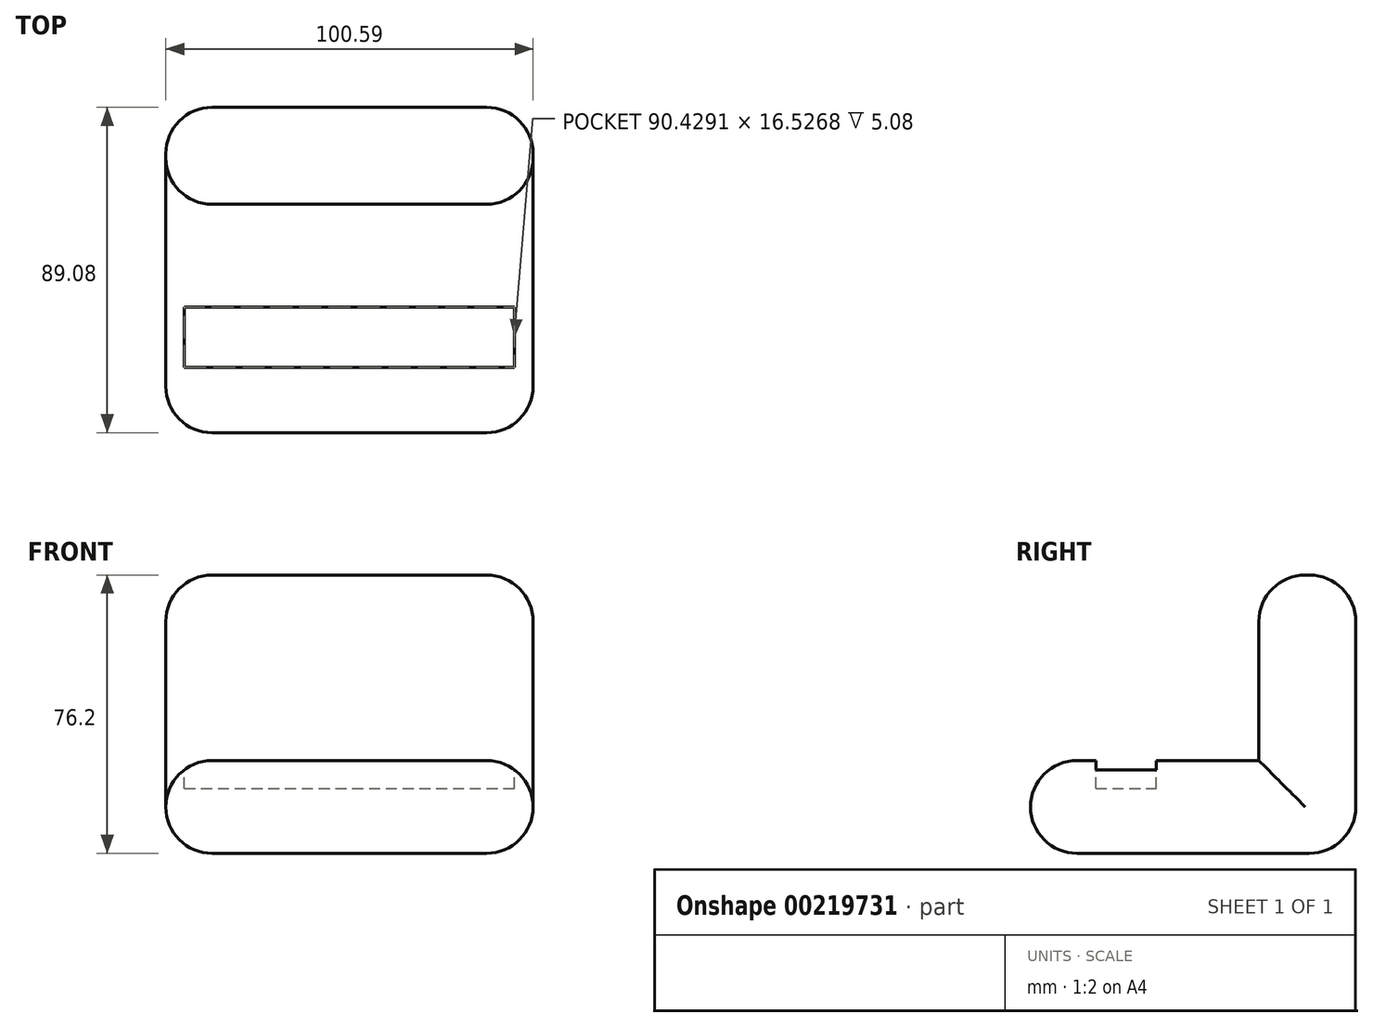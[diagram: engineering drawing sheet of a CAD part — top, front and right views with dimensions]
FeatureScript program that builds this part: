
annotation { "Feature Type Name" : "Feature", "Feature Type Description" : "" }
export const myFeature = defineFeature(function(context is Context, id is Id, definition is map)
    precondition{}
    {
        {
            var Q0;
            Q0=qCreatedBy(makeId("Top.planeOp"),FACE);
            var sketch = newSketch(context, id + "F0", { "sketchPlane" : qUnion([Q0])});
            skLineSegment(sketch, "E0.bottom", {"start": v(-49.16, -34.38) * mm, "end": v(51.43, -34.38) * mm});
            skLineSegment(sketch, "E0.top", {"start": v(-49.16, 54.7) * mm, "end": v(51.43, 54.7) * mm});
            skLineSegment(sketch, "E0.left", {"start": v(-49.16, -34.38) * mm, "end": v(-49.16, 54.7) * mm});
            skLineSegment(sketch, "E0.right", {"start": v(51.43, -34.38) * mm, "end": v(51.43, 54.7) * mm});
            skSolve(sketch);
        }
        {
            var Q0;
            Q0=makeQuery(id+"F0.imprint","IMPRINT",FACE,{"disambiguationData":[TD([[makeQuery(id+"F0.imprint","IMPRINT",EDGE,{"derivedFrom":sQuery(id+"F0.wireOp",EDGE,"E0.bottom")}),1.0]])]});
            extrude(context, id + "F1", {"entities" : qUnion([Q0]), "depth" : 25.4 * mm});
        }
        {
            var Q0;
            Q0=makeQuery(id+"F1.opExtrude","CAP_FACE",FACE,{"disambiguationData":[OSD([sQuery(id+"F0.wireOp",EDGE,"E0.bottom"),sQuery(id+"F0.wireOp",EDGE,"E0.top"),sQuery(id+"F0.wireOp",EDGE,"E0.left"),sQuery(id+"F0.wireOp",EDGE,"E0.right")])],"isStart":false});
            var sketch = newSketch(context, id + "F2", { "sketchPlane" : qUnion([Q0])});
            skLineSegment(sketch, "E1.bottom", {"start": v(-49.16, 28.15) * mm, "end": v(51.43, 28.15) * mm});
            skLineSegment(sketch, "E1.top", {"start": v(-49.16, 54.7) * mm, "end": v(51.43, 54.7) * mm});
            skLineSegment(sketch, "E1.left", {"start": v(-49.16, 28.15) * mm, "end": v(-49.16, 54.7) * mm});
            skLineSegment(sketch, "E1.right", {"start": v(51.43, 28.15) * mm, "end": v(51.43, 54.7) * mm});
            skSolve(sketch);
        }
        {
            var Q0;
            Q0=makeQuery(id+"F2.imprint","IMPRINT",FACE,{"disambiguationData":[TD([[makeQuery(id+"F2.imprint","IMPRINT",EDGE,{"derivedFrom":sQuery(id+"F2.wireOp",EDGE,"E1.bottom")}),1.0]])]});
            extrude(context, id + "F3", {"entities" : qUnion([Q0]), "operationType" : NewBodyOperationType.ADD, "depth" : 50.8 * mm});
        }
        {
            var Q0;
            Q0=makeQuery(id+"F1.opExtrude","CAP_FACE",FACE,{"disambiguationData":[OSD([sQuery(id+"F0.wireOp",EDGE,"E0.bottom"),sQuery(id+"F0.wireOp",EDGE,"E0.top"),sQuery(id+"F0.wireOp",EDGE,"E0.left"),sQuery(id+"F0.wireOp",EDGE,"E0.right")])],"isStart":false});
            var sketch = newSketch(context, id + "F4", { "sketchPlane" : qUnion([Q0])});
            skLineSegment(sketch, "E2.bottom", {"start": v(-44.08, -16.53) * mm, "end": v(46.35, -16.53) * mm});
            skLineSegment(sketch, "E2.top", {"start": v(-44.08, 0) * mm, "end": v(46.35, 0) * mm});
            skLineSegment(sketch, "E2.left", {"start": v(-44.08, -16.53) * mm, "end": v(-44.08, 0) * mm});
            skLineSegment(sketch, "E2.right", {"start": v(46.35, -16.53) * mm, "end": v(46.35, 0) * mm});
            skSolve(sketch);
        }
        {
            var Q0;
            Q0=makeQuery(id+"F4.imprint","IMPRINT",FACE,{"disambiguationData":[TD([[makeQuery(id+"F4.imprint","IMPRINT",EDGE,{"derivedFrom":sQuery(id+"F4.wireOp",EDGE,"E2.bottom")}),1.0]])]});
            extrude(context, id + "F5", {"entities" : qUnion([Q0]), "operationType" : NewBodyOperationType.REMOVE, "oppositeDirection" : true, "depth" : 7.62 * mm});
        }
        {
            var Q0;
            Q0=makeQuery(id+"F1.opExtrude","CAP_EDGE",EDGE,{"disambiguationData":[OSD([sQuery(id+"F0.wireOp",EDGE,"E0.bottom")])],"isStart":false});
            var Q1;
            Q1=makeQuery(id+"F1.opExtrude","SWEPT_EDGE",EDGE,{"disambiguationData":[OSD([sQuery(id+"F0.wireOp",EDGE,"E0.bottom"),sQuery(id+"F0.wireOp",EDGE,"E0.right")])]});
            var Q2;
            Q2=makeQuery(id+"F1.opExtrude","CAP_EDGE",EDGE,{"disambiguationData":[OSD([sQuery(id+"F0.wireOp",EDGE,"E0.bottom")])],"isStart":true});
            var Q3;
            Q3=makeQuery(id+"F1.opExtrude","SWEPT_EDGE",EDGE,{"disambiguationData":[OSD([sQuery(id+"F0.wireOp",EDGE,"E0.bottom"),sQuery(id+"F0.wireOp",EDGE,"E0.left")])]});
            var Q4;
            Q4=makeQuery(id+"F1.opExtrude","CAP_EDGE",EDGE,{"disambiguationData":[OSD([sQuery(id+"F0.wireOp",EDGE,"E0.left")])],"isStart":false});
            var Q5;
            Q5=makeQuery(id+"F3.opExtrude","CAP_EDGE",EDGE,{"disambiguationData":[OSD([sQuery(id+"F2.wireOp",EDGE,"E1.bottom")])],"isStart":false});
            var Q6;
            Q6=makeQuery(id+"F3.opExtrude","SWEPT_EDGE",EDGE,{"disambiguationData":[OSD([sQuery(id+"F0.wireOp",EDGE,"E0.left"),sQuery(id+"F2.wireOp",EDGE,"E1.bottom"),sQuery(id+"F2.wireOp",EDGE,"E1.left")])]});
            var Q7;
            Q7=makeQuery(id+"F3.opExtrude","CAP_EDGE",EDGE,{"disambiguationData":[OSD([sQuery(id+"F2.wireOp",EDGE,"E1.bottom")])],"isStart":true});
            var Q8;
            Q8=makeQuery(id+"F3.opExtrude","SWEPT_EDGE",EDGE,{"disambiguationData":[OSD([sQuery(id+"F0.wireOp",EDGE,"E0.right"),sQuery(id+"F2.wireOp",EDGE,"E1.bottom"),sQuery(id+"F2.wireOp",EDGE,"E1.right")])]});
            var Q9;
            Q9=makeQuery(id+"F1.opExtrude","CAP_EDGE",EDGE,{"disambiguationData":[OSD([sQuery(id+"F0.wireOp",EDGE,"E0.right")])],"isStart":true});
            var Q10;
            Q10=makeQuery(id+"F1.opExtrude","CAP_EDGE",EDGE,{"disambiguationData":[OSD([sQuery(id+"F0.wireOp",EDGE,"E0.right")])],"isStart":false});
            var Q11;
            Q11=makeQuery(id+"F3.boolean.opBoolean","MERGE",EDGE,{"derivedFrom":[makeQuery(id+"F1.opExtrude","SWEPT_EDGE",EDGE,{"disambiguationData":[OSD([sQuery(id+"F0.wireOp",EDGE,"E0.top"),sQuery(id+"F0.wireOp",EDGE,"E0.right")])]}),makeQuery(id+"F3.opExtrude","SWEPT_EDGE",EDGE,{"disambiguationData":[OSD([sQuery(id+"F2.wireOp",EDGE,"E1.top"),sQuery(id+"F2.wireOp",EDGE,"E1.right")])]})]});
            var Q12;
            Q12=makeQuery(id+"F3.opExtrude","CAP_EDGE",EDGE,{"disambiguationData":[OSD([sQuery(id+"F2.wireOp",EDGE,"E1.right")])],"isStart":false});
            var Q13;
            Q13=makeQuery(id+"F3.opExtrude","CAP_EDGE",EDGE,{"disambiguationData":[OSD([sQuery(id+"F2.wireOp",EDGE,"E1.top")])],"isStart":false});
            var Q14;
            Q14=makeQuery(id+"F3.opExtrude","CAP_EDGE",EDGE,{"disambiguationData":[OSD([sQuery(id+"F2.wireOp",EDGE,"E1.left")])],"isStart":false});
            var Q15;
            Q15=makeQuery(id+"F1.opExtrude","CAP_EDGE",EDGE,{"disambiguationData":[OSD([sQuery(id+"F0.wireOp",EDGE,"E0.left")])],"isStart":true});
            var Q16;
            Q16=makeQuery(id+"F3.boolean.opBoolean","MERGE",EDGE,{"derivedFrom":[makeQuery(id+"F1.opExtrude","SWEPT_EDGE",EDGE,{"disambiguationData":[OSD([sQuery(id+"F0.wireOp",EDGE,"E0.top"),sQuery(id+"F0.wireOp",EDGE,"E0.left")])]}),makeQuery(id+"F3.opExtrude","SWEPT_EDGE",EDGE,{"disambiguationData":[OSD([sQuery(id+"F2.wireOp",EDGE,"E1.top"),sQuery(id+"F2.wireOp",EDGE,"E1.left")])]})]});
            var Q17;
            Q17=makeQuery(id+"F1.opExtrude","CAP_EDGE",EDGE,{"disambiguationData":[OSD([sQuery(id+"F0.wireOp",EDGE,"E0.top")])],"isStart":true});
            fillet(context, id + "F6", {"entities" : qUnion([Q0, Q1, Q2, Q3, Q4, Q5, Q6, Q7, Q8, Q9, Q10, Q11, Q12, Q13, Q14, Q15, Q16, Q17]), "radius" : 12.7 * mm, "tangentPropagation" : true, "allowEdgeOverflow" : false});
        }
    });
